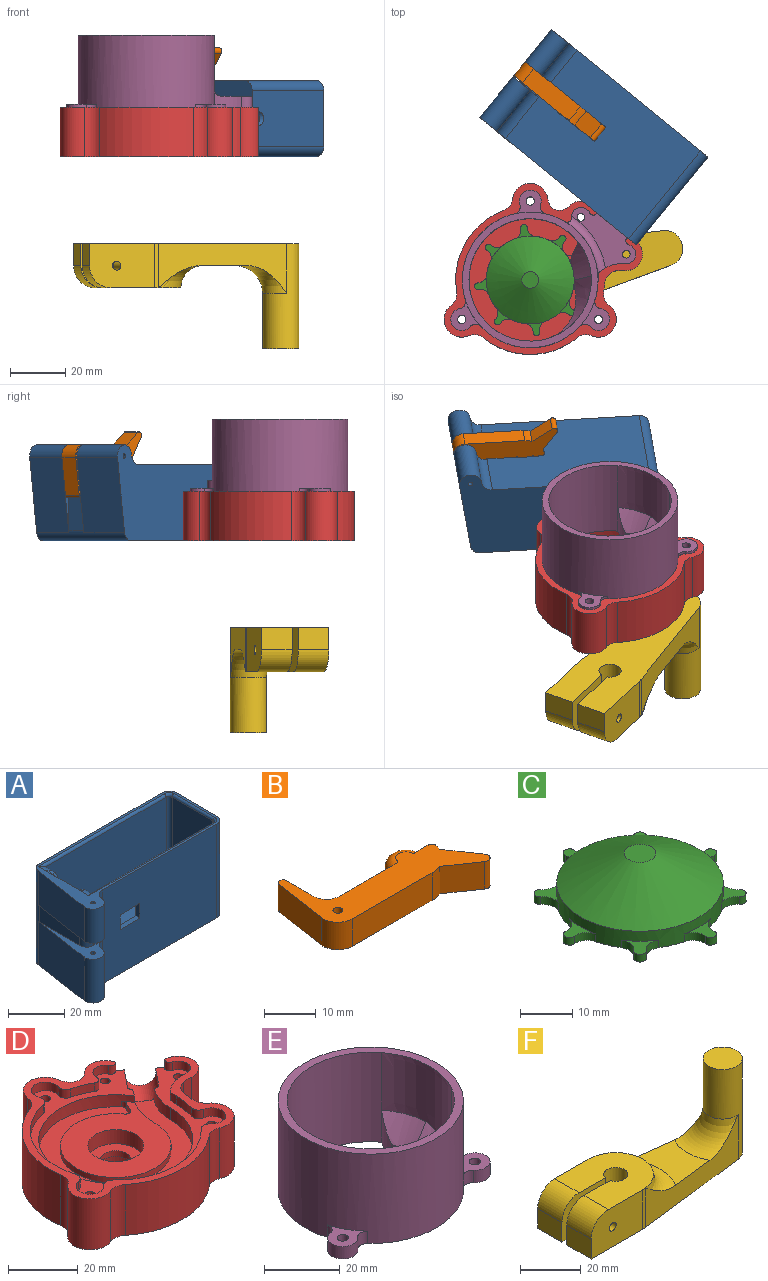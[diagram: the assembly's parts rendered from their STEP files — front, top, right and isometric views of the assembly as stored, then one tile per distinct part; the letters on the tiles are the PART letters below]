
ASSEMBLY  parts=6 mates=11
PART A: 56 faces, bbox 73x34.6x41 mm
  f0: plane 27.06x19mm, normal (-0.99,0.15,0), area 519.7mm2, adj f2,f6,f47,f55
  f1: cylinder r=4mm len=19mm, axis (0,0,-1), area 111.1mm2, adj f2,f5,f47,f55
  f2: cylinder r=4mm len=19mm, axis (0,0,-1), area 241.6mm2, adj f0,f1,f47,f55
  f3: cylinder r=0.79mm len=19mm, axis (0,0,-1), area 94.8mm2, adj f47,f55
  f4: cylinder r=0.79mm len=15mm, axis (0,0,-1), area 74.8mm2, adj f25,f54
  f5: plane 62x41mm, normal (0,-1,0), area 2325.6mm2, adj f1,f9,f10,f25,f31,f32,f33,f34
  f6: cylinder r=3.5mm len=41mm, axis (0,0,-1), area 208mm2, adj f0,f8,f13,f25,f47,f52,f54,f55
  f7: plane 60.95x29mm, normal (0,1,0), area 1668.8mm2, adj f21,f22,f26,f31,f32,f33,f34,f37
  f8: plane 20.5x7mm, normal (-1,0,0), area 143.5mm2, adj f6,f9,f54,f55
  f9: cylinder r=3.5mm len=7mm, axis (0,0,-1), area 38.5mm2, adj f5,f8,f54,f55
  f10: cylinder r=3.5mm len=41mm, axis (0,0,-1), area 225.4mm2, adj f5,f11,f25,f47
  f11: plane 41x20.5mm, normal (1,0,0), area 821.6mm2, adj f10,f12,f25,f47,f53
  f12: cylinder r=3.5mm len=41mm, axis (0,0,-1), area 225.4mm2, adj f11,f13,f25,f47
  f13: plane 62x41mm, normal (0,1,0), area 2542mm2, adj f6,f12,f25,f47
  f14: plane 30x19mm, normal (1,0,0), area 351mm2, adj f15,f24,f25,f26,f35,f38
  f15: plane 26.25x2.25mm, normal (0,-1,0), area 59.1mm2, adj f14,f16,f26,f38
  f16: cylinder r=1.5mm len=26.25mm, axis (0,0,-1), area 61.9mm2, adj f15,f17,f26,f39
  f17: plane 26.25x4.5mm, normal (1,0,0), area 118.1mm2, adj f16,f18,f26,f40
  f18: plane 60.95x29mm, normal (0,-1,0), area 1733.8mm2, adj f17,f19,f26,f40,f45
  f19: cylinder r=1.5mm len=29mm, axis (0,0,-1), area 68.3mm2, adj f18,f20,f26,f44
  f20: plane 29x20.5mm, normal (-1,0,0), area 594.5mm2, adj f19,f21,f26,f43
  f21: cylinder r=1.5mm len=29mm, axis (0,0,-1), area 68.3mm2, adj f7,f20,f26,f42
  f22: plane 26.25x4.5mm, normal (1,0,0), area 118.1mm2, adj f7,f23,f26,f37
  f23: cylinder r=1.5mm len=26.25mm, axis (0,0,-1), area 61.9mm2, adj f22,f24,f26,f36
  f24: plane 26.25x2.25mm, normal (0,1,0), area 59.1mm2, adj f14,f23,f26,f35
  f25: plane 73x34.63mm, normal (0,0,1), area 303.6mm2, adj f4,f5,f6,f10,f11,f12,f13,f14
  f26: plane 65x23.5mm, normal (0,0,1), area 934.4mm2, adj f7,f14,f15,f16,f17,f18,f19,f20
  f27: cylinder r=6.75mm len=13.5mm, axis (0,0,1), area 63.6mm2, adj f26,f28,f30,f46
  f28: plane 30x3mm, normal (0,-1,0), area 90mm2, adj f26,f27,f29,f46
  f29: cylinder r=6.75mm len=13.5mm, axis (0,0,1), area 63.6mm2, adj f26,f28,f30,f46
  f30: plane 30x3mm, normal (0,1,0), area 90mm2, adj f26,f27,f29,f46
  f31: plane 10x2mm, normal (0,0,1), area 20mm2, adj f5,f7,f32,f33
  f32: plane 6.5x2mm, normal (1,0,0), area 13mm2, adj f5,f7,f31,f34
  f33: plane 6.5x2mm, normal (-1,0,0), area 13mm2, adj f5,f7,f31,f34
  f34: plane 10x2mm, normal (0,0,-1), area 20mm2, adj f5,f7,f32,f33
  f35: cylinder r=3.75mm len=3.75mm, axis (1,0,0), area 8.4mm2, adj f14,f24,f36
  f36: bspline ~4.43x3.75mm, area 9.4mm2, adj f23,f35,f37
  f37: cylinder r=3.75mm len=5.5mm, axis (0,-1,0), area 22.8mm2, adj f7,f22,f25,f36,f41
  f38: cylinder r=3.75mm len=3.75mm, axis (-1,0,0), area 8.4mm2, adj f14,f15,f39
  f39: bspline ~4.43x3.75mm, area 9.4mm2, adj f16,f38,f40
  f40: cylinder r=3.75mm len=5.5mm, axis (0,-1,0), area 22.8mm2, adj f17,f18,f25,f39,f45
  f41: cylinder r=1mm len=63.5mm, axis (1,0,0), area 97.6mm2, adj f7,f25,f37,f42
  f42: torus R=2.5mm, axis (0,0,1), area 4.6mm2, adj f21,f25,f41,f43
  f43: cylinder r=1mm len=20.5mm, axis (0,1,0), area 32.2mm2, adj f20,f25,f42,f44
  f44: torus R=2.5mm, axis (0,0,1), area 4.6mm2, adj f19,f25,f43,f45
  f45: cylinder r=1mm len=63.5mm, axis (-1,0,0), area 97.6mm2, adj f18,f25,f40,f44
  f46: plane 43.5x13.5mm, normal (0,0,1), area 497.9mm2, adj f27,f28,f29,f30,f48
  f47: plane 73x34.63mm, normal (0,0,-1), area 1933.7mm2, adj f0,f1,f2,f3,f5,f6,f10,f11
  f48: cylinder r=4mm len=8mm, axis (0,0,1), area 194.3mm2, adj f46,f47,f49
  f49: cylinder r=1.45mm len=6.52mm, axis (1,0,0), area 58.2mm2, adj f48,f53
  f50: cylinder r=4mm len=15mm, axis (0,0,-1), area 87.7mm2, adj f5,f25,f51,f54
  f51: cylinder r=4mm len=15mm, axis (0,0,-1), area 190.8mm2, adj f25,f50,f52,f54
  f52: plane 27.06x15mm, normal (-0.99,0.15,0), area 410.3mm2, adj f6,f25,f51,f54
  f53: cone r=1.45mm half-angle=45deg, axis (1,0,0), area 17.3mm2, adj f11,f49
  f54: plane 31.64x11.95mm, normal (0,0,-1), area 96.9mm2, adj f4,f5,f6,f8,f9,f50,f51,f52
  f55: plane 31.64x11.95mm, normal (0,0,1), area 96.9mm2, adj f0,f1,f2,f3,f5,f6,f8,f9
PART B: 20 faces, bbox 37.6x23.8x6.5 mm
  f0: plane 37.63x23.77mm, normal (0,0,1), area 292.8mm2, adj f1,f2,f3,f4,f5,f6,f7,f8
  f1: plane 13.58x6.5mm, normal (-0.99,0.15,0), area 89.3mm2, adj f0,f2,f12,f17
  f2: cylinder r=4mm len=6.5mm, axis (0,0,-1), area 44.7mm2, adj f0,f1,f3,f12
  f3: plane 21.75x6.5mm, normal (0,-1,0), area 141.4mm2, adj f0,f2,f4,f12
  f4: cylinder r=7.13mm len=6.5mm, axis (0,0,-1), area 17.3mm2, adj f0,f3,f5,f12
  f5: plane 7.29x6.5mm, normal (-0.57,-0.82,0), area 57.5mm2, adj f0,f4,f6,f12
  f6: cylinder r=1.27mm len=6.5mm, axis (0,0,-1), area 22.9mm2, adj f0,f5,f7,f12
  f7: plane 7.29x6.5mm, normal (0.82,0.57,0), area 57.5mm2, adj f0,f6,f8,f12
  f8: cylinder r=7.13mm len=6.5mm, axis (0,0,-1), area 9.7mm2, adj f0,f7,f9,f12
  f9: cylinder r=1mm len=6.5mm, axis (0,0,-1), area 11.3mm2, adj f0,f8,f10,f12
  f10: plane 6.5x4.05mm, normal (0,1,0), area 15mm2, adj f0,f9,f11,f12,f18,f19
  f11: cylinder r=4mm len=8mm, axis (0,0,-1), area 31.4mm2, adj f10,f14,f18,f19
  f12: plane 37.63x23.77mm, normal (0,0,-1), area 292.8mm2, adj f1,f2,f3,f4,f5,f6,f7,f8
  f13: cylinder r=0.95mm len=6.5mm, axis (0,0,-1), area 38.9mm2, adj f0,f12
  f14: plane 16.25x6.5mm, normal (0,1,0), area 94.3mm2, adj f0,f11,f12,f16,f18,f19
  f15: plane 6.88x6.5mm, normal (1,0,0), area 44.7mm2, adj f0,f12,f16,f17
  f16: cylinder r=3.5mm len=6.5mm, axis (0,0,-1), area 39.1mm2, adj f0,f12,f14,f15
  f17: cylinder r=1mm len=6.5mm, axis (0,0,1), area 19.5mm2, adj f0,f1,f12,f15
  f18: torus R=2mm, axis (0,0,1), area 32.3mm2, adj f0,f10,f11,f14
  f19: torus R=2mm, axis (0,0,1), area 32.3mm2, adj f10,f11,f12,f14
PART C: 42 faces, bbox 40.5x40.5x11.1 mm
  f0: plane 40.46x40.46mm, normal (0,0,-1), area 843.4mm2, adj f9,f10,f11,f12,f13,f14,f15,f16
  f1: plane 6.55x5.5mm, normal (-1,0,0), area 36mm2, adj f38,f39,f41
  f2: plane 6.24x6.24mm, normal (0,0,1), area 12.4mm2, adj f9,f16,f17,f18
  f3: plane 7.18x4.74mm, normal (0,0,1), area 12.4mm2, adj f9,f19,f20,f21
  f4: plane 6.24x6.24mm, normal (0,0,1), area 12.4mm2, adj f9,f22,f23,f24
  f5: plane 7.18x4.74mm, normal (0,0,1), area 12.4mm2, adj f9,f25,f26,f27
  f6: plane 6.24x6.24mm, normal (0,0,1), area 12.4mm2, adj f9,f28,f29,f30
  f7: plane 7.18x4.74mm, normal (0,0,1), area 12.4mm2, adj f9,f31,f32,f33
  f8: plane 7.18x4.74mm, normal (0,0,1), area 12.4mm2, adj f13,f14,f15,f35
  f9: cylinder r=15.91mm len=31.81mm, axis (0,0,-1), area 291.1mm2, adj f0,f2,f3,f4,f5,f6,f7,f10
  f10: cylinder r=3.12mm len=4.1mm, axis (0,0,-1), area 8.2mm2, adj f0,f9,f11,f34
  f11: cylinder r=1.2mm len=2.14mm, axis (0,0,-1), area 7.3mm2, adj f0,f10,f12,f34
  f12: cylinder r=3.12mm len=4.1mm, axis (0,0,-1), area 8.2mm2, adj f0,f9,f11,f34
  f13: cylinder r=3.12mm len=3.4mm, axis (0,0,-1), area 8.2mm2, adj f0,f8,f9,f14
  f14: cylinder r=1.2mm len=2.4mm, axis (0,0,-1), area 7.3mm2, adj f0,f8,f13,f15
  f15: cylinder r=3.12mm len=3.4mm, axis (0,0,-1), area 8.2mm2, adj f0,f8,f9,f14
  f16: cylinder r=3.12mm len=4.1mm, axis (0,0,-1), area 8.2mm2, adj f0,f2,f9,f17
  f17: cylinder r=1.2mm len=2.14mm, axis (0,0,-1), area 7.3mm2, adj f0,f2,f16,f18
  f18: cylinder r=3.12mm len=4.1mm, axis (0,0,-1), area 8.2mm2, adj f0,f2,f9,f17
  f19: cylinder r=3.12mm len=3.4mm, axis (0,0,-1), area 8.2mm2, adj f0,f3,f9,f20
  f20: cylinder r=1.2mm len=2.4mm, axis (0,0,-1), area 7.3mm2, adj f0,f3,f19,f21
  f21: cylinder r=3.12mm len=3.4mm, axis (0,0,-1), area 8.2mm2, adj f0,f3,f9,f20
  f22: cylinder r=3.12mm len=4.1mm, axis (0,0,-1), area 8.2mm2, adj f0,f4,f9,f23
  f23: cylinder r=1.2mm len=2.14mm, axis (0,0,-1), area 7.3mm2, adj f0,f4,f22,f24
  f24: cylinder r=3.12mm len=4.1mm, axis (0,0,-1), area 8.2mm2, adj f0,f4,f9,f23
  f25: cylinder r=3.12mm len=3.4mm, axis (0,0,-1), area 8.2mm2, adj f0,f5,f9,f26
  f26: cylinder r=1.2mm len=2.4mm, axis (0,0,-1), area 7.3mm2, adj f0,f5,f25,f27
  f27: cylinder r=3.12mm len=3.4mm, axis (0,0,-1), area 8.2mm2, adj f0,f5,f9,f26
  f28: cylinder r=3.12mm len=4.1mm, axis (0,0,-1), area 8.2mm2, adj f0,f6,f9,f29
  f29: cylinder r=1.2mm len=2.14mm, axis (0,0,-1), area 7.3mm2, adj f0,f6,f28,f30
  f30: cylinder r=3.12mm len=4.1mm, axis (0,0,-1), area 8.2mm2, adj f0,f6,f9,f29
  f31: cylinder r=3.12mm len=3.4mm, axis (0,0,-1), area 8.2mm2, adj f0,f7,f9,f32
  f32: cylinder r=1.2mm len=2.4mm, axis (0,0,-1), area 7.3mm2, adj f0,f7,f31,f33
  f33: cylinder r=3.12mm len=3.4mm, axis (0,0,-1), area 8.2mm2, adj f0,f7,f9,f32
  f34: plane 6.24x6.24mm, normal (0,0,1), area 12.4mm2, adj f9,f10,f11,f12
  f35: extruded ~7.18x2.33mm, area 16.8mm2, adj f8,f9,f37
  f36: plane 6x6mm, normal (0,0,1), area 28.3mm2, adj f37
  f37: cone r=3mm half-angle=61.5deg, axis (0,0,-1), area 872.1mm2, adj f9,f35,f36
  f38: cylinder r=4mm len=8mm, axis (0,0,-1), area 139.7mm2, adj f0,f1,f39,f40
  f39: plane 8x6.3mm, normal (0,0,-1), area 42.5mm2, adj f1,f38
  f40: extruded ~6.55x2.5mm, area 19.2mm2, adj f0,f38,f41
  f41: plane 6.55x1.7mm, normal (0,0,-1), area 7.8mm2, adj f1,f40
PART D: 67 faces, bbox 71.8x61.9x17.9 mm
  f0: plane 0.79x0.02mm, normal (0.63,0.78,0), area 0mm2, adj f8,f63
  f1: plane 0.61x0.5mm, normal (0.63,0.78,0), area 0mm2, adj f9,f63
  f2: plane 66.96x57.11mm, normal (0,0,1), area 649.2mm2, adj f4,f8,f10,f11,f12,f13,f14,f15
  f3: cylinder r=4.5mm len=9mm, axis (0,0,-1), area 56.5mm2, adj f19,f20
  f4: cylinder r=22.16mm len=14.53mm, axis (0,0,1), area 38mm2, adj f2,f5,f9,f13,f18,f61,f63
  f5: cylinder r=15.91mm len=31.81mm, axis (0,0,1), area 179.9mm2, adj f4,f9,f18,f64
  f6: cylinder r=24.56mm len=3mm, axis (0,0,-1), area 6.7mm2, adj f9,f18,f64,f65
  f7: cylinder r=8mm len=16mm, axis (0,0,1), area 251.3mm2, adj f18,f19
  f8: cylinder r=15.91mm len=10.6mm, axis (0,0,1), area 46.7mm2, adj f0,f2,f9,f13,f63
  f9: plane 48.36x44.31mm, normal (0,0,1), area 758.6mm2, adj f1,f4,f5,f6,f8,f13,f63,f64
  f10: cylinder r=1.5mm len=14.88mm, axis (0,0,-1), area 140.2mm2, adj f2,f66
  f11: cylinder r=1.5mm len=14.88mm, axis (0,0,-1), area 140.2mm2, adj f2,f66
  f12: cylinder r=1.5mm len=14.88mm, axis (0,0,-1), area 140.2mm2, adj f2,f66
  f13: cylinder r=22.16mm len=44.31mm, axis (0,0,1), area 533.6mm2, adj f2,f4,f8,f9,f18,f65
  f14: plane 14.88x11.19mm, normal (0.63,0.78,0), area 170.4mm2, adj f2,f41,f49,f62,f66
  f15: cylinder r=1.4mm len=14.88mm, axis (0,0,-1), area 130.8mm2, adj f2,f66
  f16: cylinder r=1.4mm len=14.88mm, axis (0,0,-1), area 130.8mm2, adj f2,f66
  f17: cylinder r=8mm len=16mm, axis (0,0,-1), area 282.7mm2, adj f20,f66
  f18: plane 34.94x31.81mm, normal (0,0,1), area 616.8mm2, adj f4,f5,f6,f7,f13,f64,f65
  f19: plane 16x16mm, normal (0,0,1), area 137.4mm2, adj f3,f7
  f20: plane 16x16mm, normal (0,0,-1), area 137.4mm2, adj f3,f17
  f21: cylinder r=3.5mm len=6.87mm, axis (0,0,-1), area 31.2mm2, adj f2,f32,f33,f50
  f22: cylinder r=4mm len=7.94mm, axis (0,0,-1), area 46mm2, adj f2,f23,f36,f50
  f23: cylinder r=2.5mm len=3.74mm, axis (0,0,-1), area 12.7mm2, adj f2,f22,f24,f50
  f24: cylinder r=24.56mm len=35.88mm, axis (0,0,-1), area 120.7mm2, adj f2,f23,f25,f50
  f25: cylinder r=2.5mm len=3.74mm, axis (0,0,-1), area 12.7mm2, adj f2,f24,f26,f50
  f26: cylinder r=4mm len=7.94mm, axis (0,0,-1), area 46mm2, adj f2,f25,f27,f50
  f27: cylinder r=2.5mm len=3.19mm, axis (0,0,-1), area 12.7mm2, adj f2,f26,f28,f50
  f28: cylinder r=24.56mm len=31.07mm, axis (0,0,-1), area 120.7mm2, adj f2,f27,f29,f50
  f29: cylinder r=2.5mm len=3.28mm, axis (0,0,-1), area 12.7mm2, adj f2,f28,f30,f50
  f30: cylinder r=4mm len=8mm, axis (0,0,-1), area 46mm2, adj f2,f29,f37,f50
  f31: cylinder r=3.5mm len=6.61mm, axis (0,0,-1), area 28.7mm2, adj f2,f39,f40,f50
  f32: cylinder r=1.5mm len=3mm, axis (0,0,-1), area 8.5mm2, adj f2,f21,f50,f51
  f33: cylinder r=12mm len=9.57mm, axis (0,0,-1), area 31.3mm2, adj f2,f21,f34,f50
  f34: cylinder r=13.51mm len=3mm, axis (0,0,-1), area 7.7mm2, adj f2,f33,f35,f50
  f35: cylinder r=24.56mm len=7.15mm, axis (0,0,-1), area 21.8mm2, adj f2,f34,f36,f50
  f36: cylinder r=2.5mm len=3.19mm, axis (0,0,-1), area 12.7mm2, adj f2,f22,f35,f50
  f37: cylinder r=2.5mm len=3.28mm, axis (0,0,-1), area 12.7mm2, adj f2,f30,f38,f50
  f38: cylinder r=24.56mm len=7.07mm, axis (0,0,-1), area 23mm2, adj f2,f37,f39,f50
  f39: cylinder r=1.5mm len=3mm, axis (0,0,-1), area 9.8mm2, adj f2,f31,f38,f50
  f40: cylinder r=1.5mm len=3mm, axis (0,0,-1), area 8.5mm2, adj f2,f31,f50,f52
  f41: cylinder r=5.9mm len=17.88mm, axis (0,0,-1), area 220.9mm2, adj f14,f50,f52,f54,f66
  f42: cylinder r=6.4mm len=17.88mm, axis (0,0,-1), area 332.7mm2, adj f50,f53,f55,f66
  f43: cylinder r=26.96mm len=29.54mm, axis (0,0,-1), area 660.1mm2, adj f50,f55,f56,f66
  f44: cylinder r=6.4mm len=17.88mm, axis (0,0,-1), area 332.7mm2, adj f50,f56,f57,f66
  f45: cylinder r=26.96mm len=34.11mm, axis (0,0,-1), area 660.1mm2, adj f50,f57,f58,f66
  f46: cylinder r=6.4mm len=17.88mm, axis (0,0,-1), area 332.7mm2, adj f50,f58,f59,f66
  f47: cylinder r=26.96mm len=17.88mm, axis (0,0,-1), area 53mm2, adj f50,f59,f60,f66
  f48: cylinder r=9.6mm len=17.88mm, axis (0,0,-1), area 63.7mm2, adj f49,f50,f60,f66
  f49: cylinder r=5.9mm len=17.88mm, axis (0,0,-1), area 333.4mm2, adj f14,f48,f50,f51,f66
  f50: plane 71.76x61.91mm, normal (0,0,1), area 532.4mm2, adj f21,f22,f23,f24,f25,f26,f27,f28
  f51: cylinder r=0.5mm len=3mm, axis (0,0,1), area 1.4mm2, adj f2,f32,f49,f50
  f52: cylinder r=0.5mm len=3mm, axis (0,0,1), area 1.4mm2, adj f2,f40,f41,f50
  f53: cylinder r=5mm len=17.88mm, axis (0,0,1), area 90.9mm2, adj f42,f50,f54,f66
  f54: cylinder r=5mm len=17.88mm, axis (0,0,1), area 95.5mm2, adj f41,f50,f53,f66
  f55: cylinder r=5mm len=17.88mm, axis (0,0,1), area 97.6mm2, adj f42,f43,f50,f66
  f56: cylinder r=5mm len=17.88mm, axis (0,0,1), area 97.6mm2, adj f43,f44,f50,f66
  f57: cylinder r=5mm len=17.88mm, axis (0,0,1), area 97.6mm2, adj f44,f45,f50,f66
  f58: cylinder r=5mm len=17.88mm, axis (0,0,1), area 97.6mm2, adj f45,f46,f50,f66
  f59: cylinder r=5mm len=17.88mm, axis (0,0,1), area 97.6mm2, adj f46,f47,f50,f66
  f60: cylinder r=5mm len=17.88mm, axis (0,0,-1), area 111.9mm2, adj f47,f48,f50,f66
  f61: plane 0.79x0.02mm, normal (0.63,0.78,0), area 0mm2, adj f4,f63
  f62: cylinder r=4.65mm len=12.58mm, axis (0.63,0.78,0), area 143.5mm2, adj f2,f14,f63
  f63: torus R=3.15mm, axis (0.63,0.78,0), area 31.4mm2, adj f0,f1,f2,f4,f8,f9,f61,f62
  f64: cylinder r=1.5mm len=2.59mm, axis (0,0,1), area 6.3mm2, adj f5,f6,f9,f18
  f65: cylinder r=1.5mm len=2mm, axis (0,0,-1), area 3.7mm2, adj f6,f9,f13,f18
  f66: plane 71.76x61.91mm, normal (0,0,-1), area 2645.4mm2, adj f10,f11,f12,f14,f15,f16,f17,f41
PART E: 48 faces, bbox 67.7x62x30.4 mm
  f0: cylinder r=22.16mm len=44.31mm, axis (0,0,-1), area 3257mm2, adj f28,f30,f31,f33,f36,f37,f43,f44
  f1: plane 11.19x9.12mm, normal (0.63,0.78,0), area 77.4mm2, adj f10,f11,f30,f38,f39
  f2: cylinder r=24.56mm len=49.11mm, axis (0,0,-1), area 4086.9mm2, adj f3,f4,f6,f14,f15,f17,f18,f20
  f3: plane 11.1x8.64mm, normal (0,0,1), area 50.2mm2, adj f2,f15,f16,f17,f27
  f4: plane 11.13x10.79mm, normal (0,0,1), area 50.2mm2, adj f2,f18,f19,f20,f26
  f5: cylinder r=22.16mm len=10.73mm, axis (0,0,-1), area 23.4mm2, adj f30,f31,f41,f42
  f6: cylinder r=13.51mm len=10mm, axis (0,0,-1), area 23.9mm2, adj f2,f7,f30,f47
  f7: cylinder r=12mm len=9.57mm, axis (0,0,-1), area 75.5mm2, adj f6,f8,f30,f38,f47
  f8: cylinder r=3.5mm len=7mm, axis (0,0,-1), area 72.8mm2, adj f7,f9,f30,f38
  f9: cylinder r=1.5mm len=7mm, axis (0,0,-1), area 19.9mm2, adj f8,f10,f30,f38
  f10: cylinder r=0.5mm len=7mm, axis (0,0,-1), area 3.2mm2, adj f1,f9,f30,f38
  f11: cylinder r=0.5mm len=7mm, axis (0,0,-1), area 3.2mm2, adj f1,f12,f30,f38
  f12: cylinder r=1.5mm len=7mm, axis (0,0,-1), area 19.9mm2, adj f11,f13,f30,f38
  f13: cylinder r=3.5mm len=7.07mm, axis (0,0,-1), area 66.9mm2, adj f12,f14,f30,f38,f47
  f14: cylinder r=1.5mm len=10mm, axis (0,0,-1), area 27.8mm2, adj f2,f13,f30,f47
  f15: cylinder r=2.5mm len=4mm, axis (0,0,-1), area 16.9mm2, adj f2,f3,f16,f30
  f16: cylinder r=4mm len=8mm, axis (0,0,-1), area 61.3mm2, adj f3,f15,f17,f30
  f17: cylinder r=2.5mm len=4mm, axis (0,0,-1), area 16.9mm2, adj f2,f3,f16,f30
  f18: cylinder r=2.5mm len=4mm, axis (0,0,-1), area 16.9mm2, adj f2,f4,f19,f30
  f19: cylinder r=4mm len=7.94mm, axis (0,0,-1), area 61.3mm2, adj f4,f18,f20,f30
  f20: cylinder r=2.5mm len=4mm, axis (0,0,-1), area 16.9mm2, adj f2,f4,f19,f30
  f21: cylinder r=2.5mm len=4mm, axis (0,0,-1), area 16.9mm2, adj f2,f22,f30,f35
  f22: cylinder r=4mm len=7.94mm, axis (0,0,-1), area 61.3mm2, adj f21,f23,f30,f35
  f23: cylinder r=2.5mm len=4mm, axis (0,0,-1), area 16.9mm2, adj f2,f22,f30,f35
  f24: cylinder r=1.4mm len=7mm, axis (0,0,-1), area 61.6mm2, adj f30,f38
  f25: cylinder r=1.5mm len=4mm, axis (0,0,-1), area 37.7mm2, adj f30,f35
  f26: cylinder r=1.5mm len=4mm, axis (0,0,-1), area 37.7mm2, adj f4,f30
  f27: cylinder r=1.5mm len=4mm, axis (0,0,-1), area 37.7mm2, adj f3,f30
  f28: cylinder r=15.91mm len=10.6mm, axis (0,0,-1), area 22.5mm2, adj f0,f30,f31,f41
  f29: cylinder r=1.4mm len=7mm, axis (0,0,-1), area 61.6mm2, adj f30,f38
  f30: plane 67.2x57.35mm, normal (0,0,-1), area 669.2mm2, adj f0,f1,f2,f5,f6,f7,f8,f9
  f31: plane 33.38x14.16mm, normal (0,0,-1), area 138.4mm2, adj f0,f5,f28,f32,f34,f40,f41,f42
  f32: cylinder r=22.16mm len=4.17mm, axis (0,0,-1), area 4.3mm2, adj f31,f34,f43,f44,f45
  f33: cylinder r=24.56mm len=10.4mm, axis (0,0,-1), area 54.8mm2, adj f0,f30,f34,f46
  f34: cylinder r=15.91mm len=6.68mm, axis (0,0,-1), area 21mm2, adj f30,f31,f32,f33,f42,f46
  f35: plane 11.13x10.79mm, normal (0,0,1), area 50.2mm2, adj f2,f21,f22,f23,f25
  f36: extruded ~24.86x22.8mm, area 519.9mm2, adj f0,f37,f45,f46
  f37: plane 49.11x49.11mm, normal (0,0,1), area 352.2mm2, adj f0,f2,f36
  f38: plane 23.32x21.81mm, normal (0,0,1), area 202mm2, adj f1,f7,f8,f9,f10,f11,f12,f13
  f39: cylinder r=4.65mm len=12.37mm, axis (0.63,0.78,0), area 104.9mm2, adj f1,f30,f41
  f40: plane 0.61x0.5mm, normal (0.63,0.78,0), area 0mm2, adj f31,f41
  f41: torus R=3.15mm, axis (-0.63,-0.78,0), area 19.1mm2, adj f5,f28,f30,f31,f39,f40
  f42: cylinder r=0.4mm len=2mm, axis (0,0,-1), area 2.2mm2, adj f5,f30,f31,f34
  f43: cylinder r=15mm len=17.45mm, axis (0,0,-1), area 9.2mm2, adj f0,f32,f44,f45
  f44: cone r=15.8mm half-angle=45deg, axis (0,0,-1), area 23.9mm2, adj f0,f31,f32,f43
  f45: cone r=15.8mm half-angle=45deg, axis (0,0,1), area 122.1mm2, adj f0,f32,f36,f43,f46
  f46: bspline ~16.25x9.74mm, area 86.8mm2, adj f33,f34,f36,f45
  f47: torus R=27.56mm, axis (0,0,1), area 106.8mm2, adj f2,f6,f7,f13,f14,f38
PART F: 22 faces, bbox 80.5x56.3x38 mm
  f0: cylinder r=12.5mm len=16mm, axis (0,0,-1), area 24.1mm2, adj f2,f3,f13,f16
  f1: plane 20.92x18.09mm, normal (0,0,1), area 273.4mm2, adj f2,f11,f15,f17
  f2: plane 49.28x18mm, normal (0.12,0.99,0), area 493.7mm2, adj f0,f1,f12,f13,f15,f17
  f3: plane 24x16mm, normal (0,1,0), area 362.2mm2, adj f0,f4,f13,f16,f19,f21
  f4: plane 11.35x8mm, normal (-1,0,0), area 90.8mm2, adj f3,f5,f13,f21
  f5: plane 20.17x16mm, normal (0,-1,0), area 300.9mm2, adj f4,f6,f13,f16,f19,f21
  f6: cylinder r=4mm len=16mm, axis (0,0,-1), area 364.8mm2, adj f5,f7,f13,f16
  f7: plane 20.17x16mm, normal (0,1,0), area 300.9mm2, adj f6,f8,f13,f16,f18,f20
  f8: plane 11.35x8mm, normal (-1,0,0), area 90.8mm2, adj f7,f9,f13,f20
  f9: plane 24x16mm, normal (0,-1,0), area 362.2mm2, adj f8,f10,f13,f16,f18,f20
  f10: cylinder r=12.5mm len=16mm, axis (0,0,-1), area 24.1mm2, adj f9,f11,f13,f16
  f11: plane 49.28x18mm, normal (0.12,-0.99,0), area 493.7mm2, adj f1,f10,f12,f13,f15,f17
  f12: cylinder r=6.5mm len=38mm, axis (0,0,-1), area 1156.2mm2, adj f2,f11,f13,f14,f15
  f13: plane 80.5x25mm, normal (0,0,-1), area 1526.8mm2, adj f0,f2,f3,f4,f5,f6,f7,f8
  f14: plane 13x13mm, normal (0,0,1), area 132.7mm2, adj f12
  f15: torus R=16.5mm, axis (0,0,1), area 275.8mm2, adj f1,f2,f11,f12
  f16: plane 28.5x25mm, normal (0,0,1), area 567.4mm2, adj f0,f3,f5,f6,f7,f9,f10,f17
  f17: torus R=20.5mm, axis (0,0,1), area 340.6mm2, adj f1,f2,f11,f16
  f18: cylinder r=1.6mm len=11.35mm, axis (0,-1,0), area 114.1mm2, adj f7,f9
  f19: cylinder r=1.6mm len=11.35mm, axis (0,-1,0), area 114.1mm2, adj f3,f5
  f20: cylinder r=8mm len=11.35mm, axis (0,1,0), area 142.6mm2, adj f7,f8,f9,f16
  f21: cylinder r=8mm len=11.35mm, axis (0,1,0), area 142.6mm2, adj f3,f4,f5,f16
PLACE A rot(axis=(-0.89,0.32,-0.32),96.5deg) t=(16.67,40.67,9)mm
PLACE B rot(axis=(-0.89,0.32,-0.32),96.5deg) t=(16.83,40.86,9)mm
PLACE C rot(axis=(0,0,-1),38.1deg) t=(0,0,67.87)mm
PLACE D t=(0,0,-3)mm fixed
PLACE E t=(0,0,-3)mm
PLACE F rot(axis=(0.99,0.12,0),180deg) t=(0,0,-36.2)mm
MATE cylindrical E.f0 <-> D.f43  axis (0,0,-1) through (0,0,24.63)mm
MATE cylindrical A.f48 <-> D.f62  axis (0.63,0.78,0) through (32.16,22.88,9)mm
MATE planar B.f0 <-> A.f2  axis (0.63,0.78,0) through (9.74,69.55,29.88)mm
MATE planar E.f0 <-> D.f28  axis (0,0,-1) through (0,0,10.13)mm
MATE cylindrical E.f16 <-> D.f10  axis (0,0,-1) through (0,28.56,12.13)mm
MATE cylindrical C.f38 <-> D.f3  axis (0,0,-1) through (0,0,11.87)mm
MATE planar B.f14 <-> A.f5  axis (0,0,-1) through (7.59,67.1,22.75)mm
MATE cylindrical F.f6 <-> D.f3  axis (0,0,1) through (0,0,-44.2)mm
MATE planar C.f9 <-> D.f18  axis (0,0,-1) through (0,0,7.88)mm
MATE cylindrical B.f2 <-> A.f2  axis (-0.63,-0.78,0) through (-0.75,73.9,25.88)mm
MATE planar A.f47 <-> D.f14  axis (-0.63,-0.78,0) through (9.79,35.96,9.59)mm
